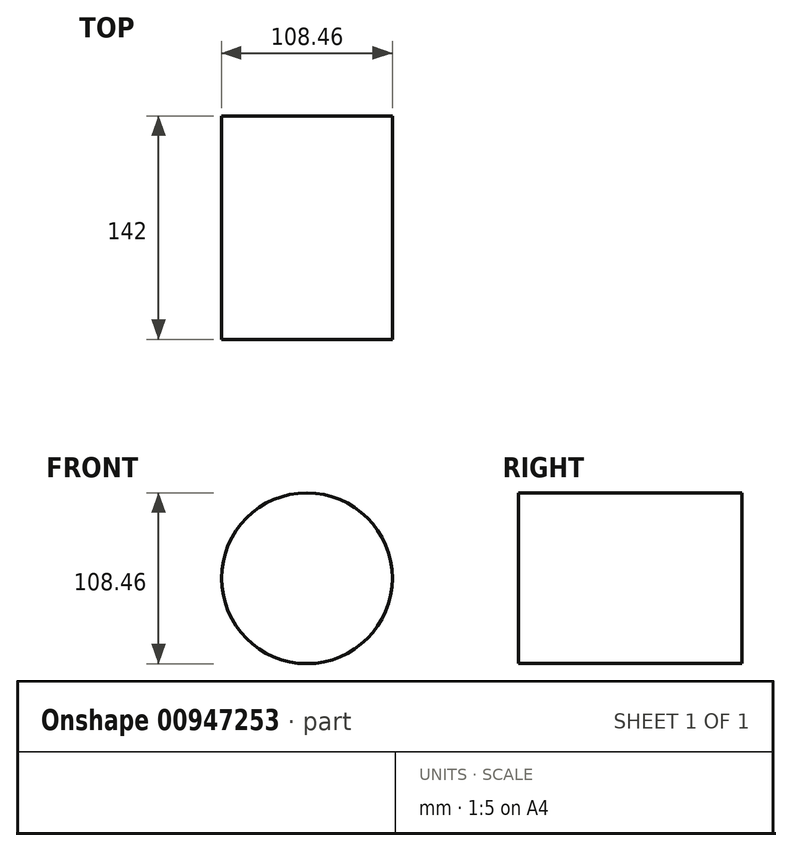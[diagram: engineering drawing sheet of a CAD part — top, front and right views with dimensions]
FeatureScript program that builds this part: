
annotation { "Feature Type Name" : "Feature", "Feature Type Description" : "" }
export const myFeature = defineFeature(function(context is Context, id is Id, definition is map)
    precondition{}
    {
        {
            var Q0;
            Q0=qCreatedBy(makeId("Front.planeOp"),FACE);
            var sketch = newSketch(context, id + "F0", { "sketchPlane" : qUnion([Q0])});
            skCircle(sketch, "E0", {"center": v(0, 0) * mm, "radius": 54.23 * mm});
            skSolve(sketch);
        }
        {
            var Q0;
            Q0=makeQuery(id+"F0.imprint","IMPRINT",FACE,{"disambiguationData":[TD([[makeQuery(id+"F0.imprint","IMPRINT",EDGE,{"derivedFrom":sQuery(id+"F0.wireOp",EDGE,"E0")}),1.0]])]});
            extrude(context, id + "F1", {"entities" : qUnion([Q0]), "depth" : 142 * mm, "offsetDistance" : 25 * mm});
        }
    });
